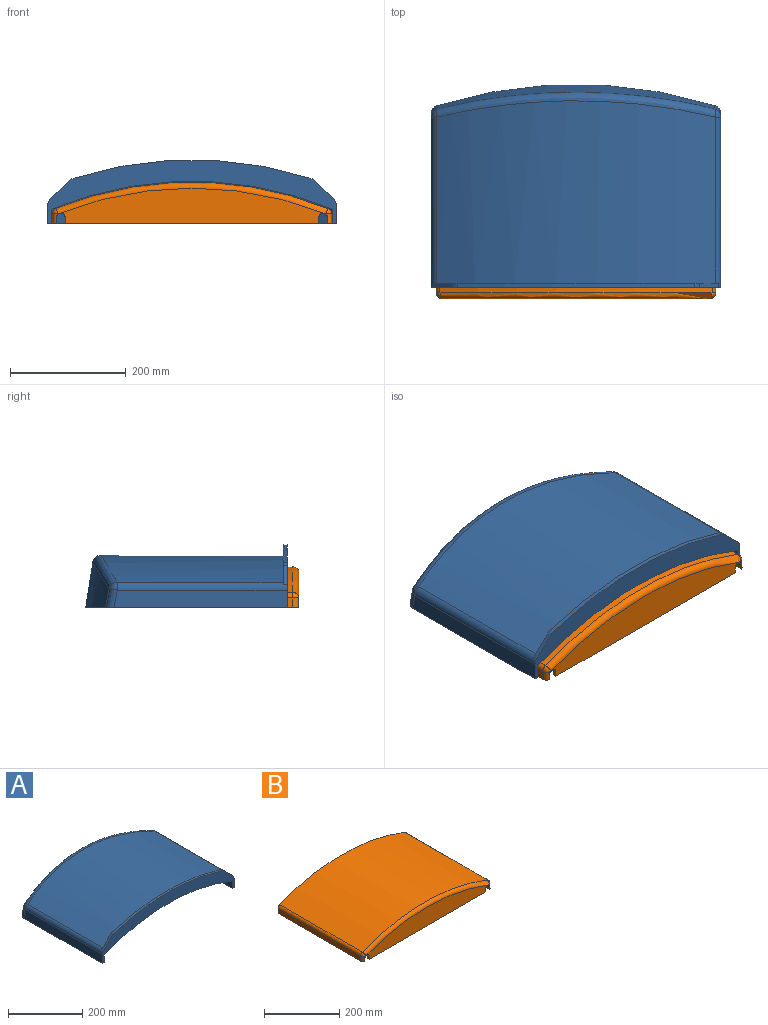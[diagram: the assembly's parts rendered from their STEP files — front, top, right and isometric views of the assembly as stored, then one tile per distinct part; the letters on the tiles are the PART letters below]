
ASSEMBLY  parts=2 mates=1
PART A: 32 faces, bbox 531.8x353.3x468.8 mm
  f0: plane 298.82x29.92mm, normal (-1,0,0), area 8818.6mm2, adj f5,f6,f21,f29,f30,f31
  f1: cylinder r=650mm len=481.1mm, axis (0,-1,0), area 141088.7mm2, adj f2,f8,f11,f17
  f2: cylinder r=15mm len=293.29mm, axis (0,-1,0), area 5200mm2, adj f1,f3,f6,f12,f14,f17
  f3: plane 298.82x29.92mm, normal (1,0,0), area 8856.5mm2, adj f2,f5,f6,f13
  f4: plane 298.82x29.92mm, normal (-1,0,0), area 8856.5mm2, adj f5,f6,f8,f9
  f5: plane 500.69x350.69mm, normal (0,0,-1), area 7833.1mm2, adj f0,f3,f4,f6,f7,f9,f13,f22
  f6: plane 500x110mm, normal (0,-1,0), area 18253.7mm2, adj f0,f2,f3,f4,f5,f8,f14,f15
  f7: cone r=801.25mm half-angle=10deg, axis (0,0,-1), area 30923.6mm2, adj f5,f9,f11,f13
  f8: cylinder r=15mm len=293.29mm, axis (0,-1,0), area 5200mm2, adj f1,f4,f6,f10,f16,f17
  f9: bspline ~468.1x100.22mm, area 605.2mm2, adj f4,f5,f7,f10
  f10: sphere r=15mm, area 147.2mm2, adj f8,f9,f11
  f11: bspline ~531.07x67.56mm, area 10168.8mm2, adj f1,f7,f10,f12
  f12: sphere r=15mm, area 196.2mm2, adj f2,f11,f13
  f13: bspline ~468.1x100.22mm, area 605.2mm2, adj f3,f5,f7,f12
  f14: plane 32.38x32.38mm, normal (0.71,0,0.71), area 320.6mm2, adj f2,f6,f17,f18
  f15: cylinder r=670mm len=410.42mm, axis (0,-1,0), area 2919.8mm2, adj f6,f17,f18,f19
  f16: plane 32.38x32.38mm, normal (-0.71,0,0.71), area 320.6mm2, adj f6,f8,f17,f19
  f17: plane 491.21x69.48mm, normal (0,1,0), area 9236.3mm2, adj f1,f2,f8,f14,f15,f16,f18,f19
  f18: cylinder r=20mm len=8.02mm, axis (0,-1,0), area 66.4mm2, adj f6,f14,f15,f17
  f19: cylinder r=20mm len=8.02mm, axis (0,-1,0), area 66.4mm2, adj f6,f15,f16,f17
  f20: cylinder r=643mm len=475.92mm, axis (0,-1,0), area 139569.2mm2, adj f21,f24,f27,f31
  f21: cylinder r=8mm len=286.29mm, axis (0,-1,0), area 2729.4mm2, adj f0,f20,f28,f31
  f22: plane 298.82x29.92mm, normal (1,0,0), area 8818.6mm2, adj f5,f6,f24,f25,f30,f31
  f23: cone r=794.36mm half-angle=10deg, axis (0,0,-1), area 30060.5mm2, adj f5,f25,f27,f29
  f24: cylinder r=8mm len=286.29mm, axis (0,-1,0), area 2729.4mm2, adj f20,f22,f26,f31
  f25: bspline ~466.88x93.61mm, area 316.5mm2, adj f5,f22,f23,f26
  f26: sphere r=8mm, area 41.9mm2, adj f24,f25,f27
  f27: bspline ~523.16x61.77mm, area 5362.5mm2, adj f20,f23,f26,f28
  f28: sphere r=8mm, area 41.9mm2, adj f21,f27,f29
  f29: bspline ~466.88x93.61mm, area 316.5mm2, adj f0,f5,f23,f28
  f30: cylinder r=633mm len=486mm, axis (0,-1,0), area 3491.6mm2, adj f0,f6,f22,f31
  f31: plane 486x58.5mm, normal (0,1,0), area 4975.5mm2, adj f0,f20,f21,f22,f24,f30
PART B: 36 faces, bbox 508.1x320x123 mm
  f0: plane 319.54x7mm, normal (0,0,-1), area 2219mm2, adj f4,f16,f17,f23
  f1: plane 438x7mm, normal (0,0,-1), area 3066mm2, adj f4,f9,f32,f34
  f2: plane 438x7mm, normal (0,0,-1), area 3066mm2, adj f3,f8,f29,f31
  f3: plane 454.26x61mm, normal (0,-1,0), area 21019.3mm2, adj f2,f6,f28,f29,f30,f31
  f4: plane 482x71mm, normal (0,1,0), area 26148.9mm2, adj f0,f1,f13,f14,f15,f16,f18,f20
  f5: cylinder r=10mm len=16.44mm, axis (0,0,1), area 213.5mm2, adj f7,f13,f15,f22,f28
  f6: torus R=621mm, axis (0,-1,0), area 7510.2mm2, adj f3,f7,f14,f19,f28,f30
  f7: sphere r=10mm, area 119mm2, adj f5,f6,f20,f28
  f8: plane 454.26x61mm, normal (0,1,0), area 21019.3mm2, adj f2,f11,f28,f29,f30,f31
  f9: plane 468x64mm, normal (0,-1,0), area 22462.2mm2, adj f1,f21,f22,f23,f25,f27,f32,f33
  f10: cylinder r=3mm len=5.94mm, axis (0,0,1), area 12.2mm2, adj f12,f22,f28
  f11: torus R=621mm, axis (0,-1,0), area 2235.8mm2, adj f8,f12,f21,f26,f28,f30
  f12: sphere r=3mm, area 10.7mm2, adj f10,f11,f27,f28
  f13: plane 319.54x7mm, normal (0,0,-1), area 2219mm2, adj f4,f5,f15,f22
  f14: cylinder r=631mm len=469.44mm, axis (0,1,0), area 149110.3mm2, adj f4,f6,f18,f20
  f15: plane 310x16.44mm, normal (-1,0,0), area 5095.6mm2, adj f4,f5,f13,f20
  f16: plane 310x16.44mm, normal (1,0,0), area 5095.6mm2, adj f0,f4,f17,f18
  f17: cylinder r=10mm len=16.44mm, axis (0,0,-1), area 213.5mm2, adj f0,f16,f19,f23,f30
  f18: cylinder r=10mm len=310mm, axis (0,1,0), area 3687.9mm2, adj f4,f14,f16,f19
  f19: sphere r=10mm, area 119mm2, adj f6,f17,f18,f30
  f20: cylinder r=10mm len=310mm, axis (0,1,0), area 3687.9mm2, adj f4,f7,f14,f15
  f21: cylinder r=624mm len=464.23mm, axis (0,1,0), area 144126.5mm2, adj f9,f11,f25,f27
  f22: plane 319.54x16.44mm, normal (1,0,0), area 5154.2mm2, adj f4,f5,f9,f10,f13,f27,f28,f33
  f23: plane 319.54x16.44mm, normal (-1,0,0), area 5154.2mm2, adj f0,f4,f9,f17,f24,f25,f30,f35
  f24: cylinder r=3mm len=5.94mm, axis (0,0,-1), area 12.2mm2, adj f23,f26,f30
  f25: cylinder r=3mm len=303mm, axis (0,1,0), area 1081.4mm2, adj f9,f21,f23,f26
  f26: sphere r=3mm, area 10.7mm2, adj f11,f24,f25,f30
  f27: cylinder r=3mm len=303mm, axis (0,1,0), area 1081.4mm2, adj f9,f12,f21,f22
  f28: cylinder r=7.5mm len=15mm, axis (0,-1,0), area 171.2mm2, adj f3,f5,f6,f7,f8,f10,f11,f12
  f29: plane 10.5x7mm, normal (-1,0,0), area 73.5mm2, adj f2,f3,f8,f28
  f30: cylinder r=7.5mm len=15mm, axis (0,-1,0), area 171.2mm2, adj f3,f6,f8,f11,f17,f19,f23,f24
  f31: plane 10.5x7mm, normal (1,0,0), area 73.5mm2, adj f2,f3,f8,f30
  f32: plane 10.5x7mm, normal (-1,0,0), area 73.5mm2, adj f1,f4,f9,f33
  f33: cylinder r=7.5mm len=15mm, axis (0,-1,0), area 164.9mm2, adj f4,f9,f22,f32
  f34: plane 10.5x7mm, normal (1,0,0), area 73.5mm2, adj f1,f4,f9,f35
  f35: cylinder r=7.5mm len=15mm, axis (0,-1,0), area 164.9mm2, adj f4,f9,f23,f34
PLACE A at identity fixed
PLACE B t=(0,280,0)mm
MATE slider A.f6 <-> B.f4  axis (0,-1,0) through (250,0,-40)mm
